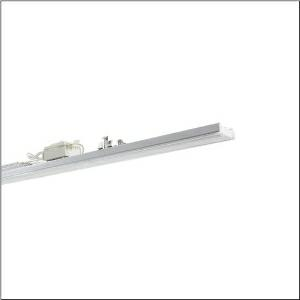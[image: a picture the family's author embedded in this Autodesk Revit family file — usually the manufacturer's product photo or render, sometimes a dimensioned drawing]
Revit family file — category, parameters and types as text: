
# Revit family: licross_21_recessed_mo_52tl12dn5axg
name_source: partatom
category: Lighting Fixtures
units: mm (PartAtom-declared; Revit-internal decimal feet)

## family parameters
Cut with Voids When Loaded = No
Host = Face
Light Source = No
Part Type = Normal
Room Calculation Point = No
Round Connector Dimension = Use Diameter
Shared = No

## types (1)
- --- (1 x LED, 10170 lm, 58 W, 5000K)
    Apparent Load = 58 VA
    CIE Flux Codes = 72 92 99 100 100
    Color Rendering = 80
    Color Temperature = 5000K
    Default Elevation = 1800 mm
    Description = Licross 21 Recessed MO, luminaire insert, of sheet steel, galvanised, coil coated, white, length: 1.500mm, width: 66mm, height: 67mm, LED rated luminous flux: 10.180lm, light colour: 850, SDCM (Standard Deviation of Colour Matching)MacAdam ≤ 3 SDCM (initial), control gear: DALI 2, with plug, 5-pole, with phase selection, mains connection: 220..240V, AC, 50/60Hz, rated input power: 58W, internal wiring halogen-free, primary optical cover: cover, of PMMA, light emission: direct distribution, primary light characteristic: symmetric, protection rating (complete): IP40, insulation class (complete): insulation class I (protective earthing), certification: CE, ENEC, VDE, UKCA, protection symbol: D if used in an environment without relevant dust loads with corresponding accessories, impact resistance: IK06, permissible ambient temperature for indoor applications: -25..+35°C, corresponds to IFS (International Featured Standards) requirements for safety and quality in the food industry, reducing of maximum allowable ambient temperature of 5°C with ceiling mounting, LABS conformity tested according to VDMA 24364:2018-05, The light source and the operating device comply with the requirements of the Ecodesign Regulation (EU) 2019/2020 and are replaceable in accordance with this regulation, packaging unit: 1 piece
    Height = 58 mm
    Lamp = 1 x LED
    Lamp Light Flux = 10170 lm
    Lamp Power = 58 W
    Lamp count = 1
    Length = 1500 mm
    Luminous efficacy = 175 lm/W
    Manufacturer = Siteco
    ModVariant = No
    Model = 52TL12DN5AXG
    Mounting Place = Ceiling
    Mounting Type = Pendant
    Number of Poles = 1
    OnlyDefault = Yes
    Power Factor = 1
    Product Name = Licross 21 Recessed MO
    Product group = luminaire insert | ceiling pendant
    ProductGroupID = 901
    Protection Class = Protection class I
    Protection Degree = IP 40
    RLX_Detail_Level = 1
    RLX_Emergency_Light_Flux = 0 lm
    RLX_Emergency_Type = 0
    RLX_Emergency_Type_DB = No
    RlxData = <blob elided: 24917 chars, md5=581d3c5e>
    Socket = socket
    Standby Power = 0 W
    System Light Flux = 10170 lm
    System Power = 58 W
    Type Comments = factory setting: luminous flux: 100 % | dim-lin: 254 | 390 mA
    Type Image = l_1296930.jpg
    URL = http://relux.com
    VarID = @adj_093461
    Voltage = 0 V
    Weight = 0.00 kg
    Width = 66 mm

## geometry (parser evidence)
native form markers: Blend x4, Sweep x12
no freeform markers — native parametric forms only
